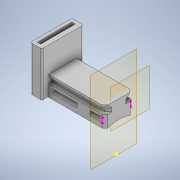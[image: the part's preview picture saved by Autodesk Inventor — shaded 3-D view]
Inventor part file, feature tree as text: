
AUTODESK INVENTOR PART (.ipt)
format: ipt  version: 2021.1 (Build 251245010, 245A)  size: 227,840 bytes
history: native  units: mm
features: move_body x4, sketch x3, extrude x2, plane x2, direct_edit x1, other x1
ambient origin geometry x8: Origin, YZ Plane, XZ Plane, XY Plane, X Axis, Y Axis, Z Axis, Center Point
bodies: Volumenkörper1 (feature_tree)
feature tree (13):
  direct_edit  "Direktbearbeitung1"
  extrude  "Extrusion1"  Depth=5.0mm TaperAngle=0.0deg
  plane  "Arbeitsebene4"
  sketch  "Skizze3"  dims[d6=0.0mm d7=0.0mm d8=-5.0mm d9=0.0mm d10=0.0mm d11=-6.75mm]
  plane  "Arbeitsebene3"
  extrude  "Extrusion2"  TaperAngle=0.0deg  [1 undecoded]
  sketch  "Skizze1"  dims[d0=0.0mm d1=0.0mm d2=15.75mm d3=5.0mm d4=0.0mm d5=0.0mm]
  sketch  "Skizze5"  dims[d12=10.0mm d13=0.0mm d16=5.5mm d17=0.0mm]
  other  "Körper1"
  move_body  "Verschieben1"
  move_body  "Verschieben2"
  move_body  "Verschieben3"
  move_body  "Verschieben4"
note: 1 required parameter value undecoded (feature->parameter linkage not recoverable at this tier; creation-order binding heuristic only, values carry confidence <= 0.55)
